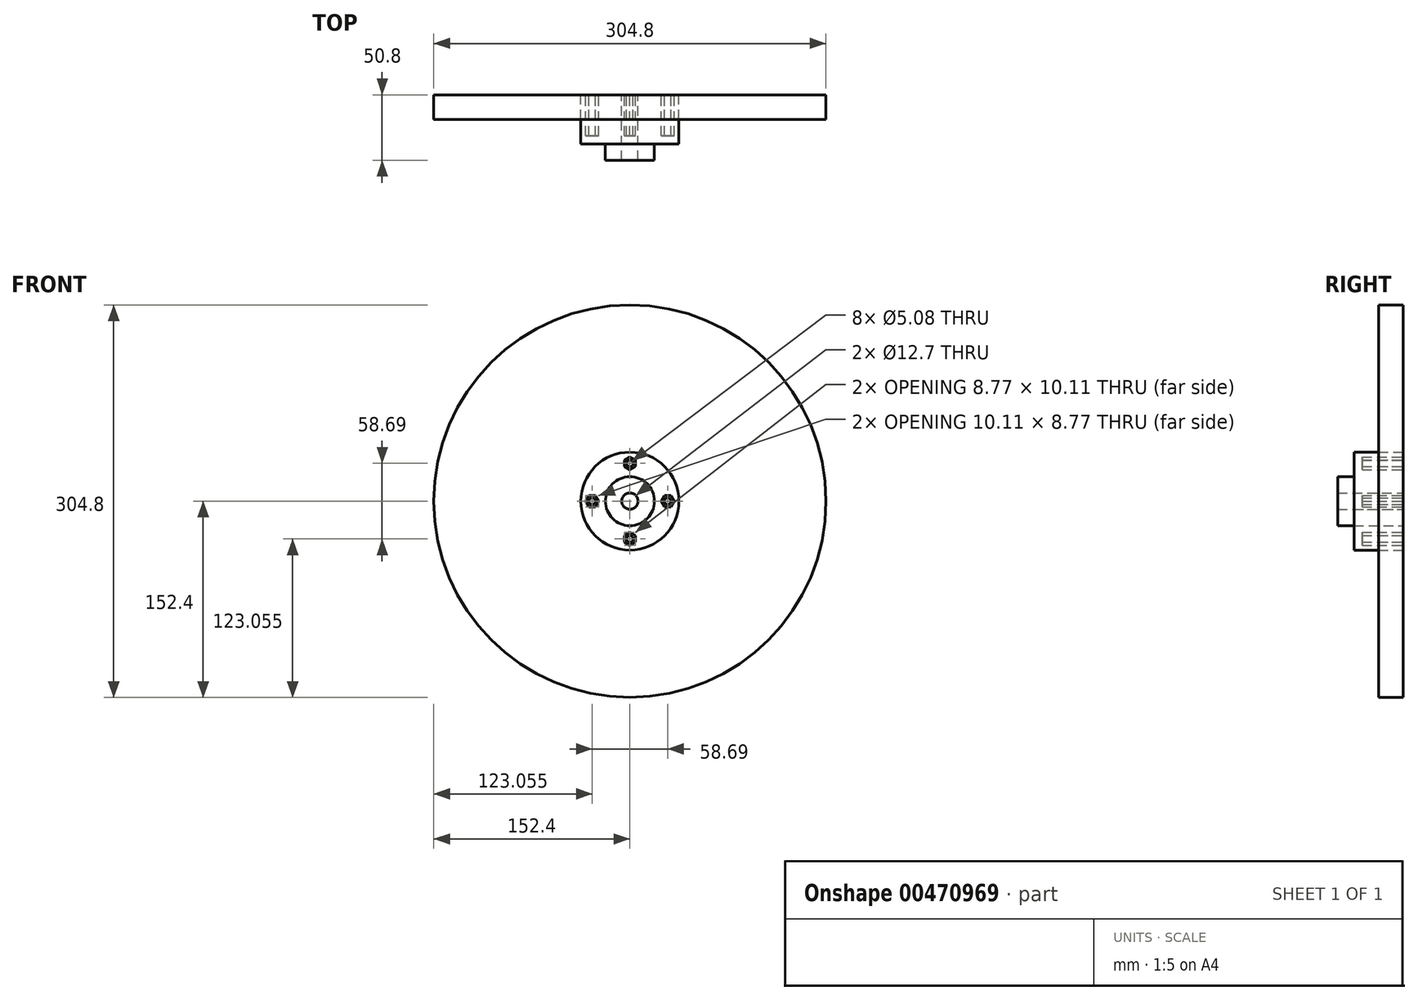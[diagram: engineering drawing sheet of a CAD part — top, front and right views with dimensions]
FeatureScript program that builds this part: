
annotation { "Feature Type Name" : "Feature", "Feature Type Description" : "" }
export const myFeature = defineFeature(function(context is Context, id is Id, definition is map)
    precondition{}
    {
        {
            var Q0;
            Q0=qCreatedBy(makeId("Front.planeOp"),FACE);
            var sketch = newSketch(context, id + "F0", { "sketchPlane" : qUnion([Q0])});
            skCircle(sketch, "E0", {"center": v(0, 0) * mm, "radius": 152.4 * mm});
            skCircle(sketch, "E1", {"center": v(0, 0) * mm, "radius": 38.1 * mm});
            skCircle(sketch, "E2", {"center": v(0, 0) * mm, "radius": 19.05 * mm});
            skCircle(sketch, "E3", {"center": v(0, 0) * mm, "radius": 6.35 * mm});
            skCircle(sketch, "E4.cCircle", {"center": v(-29.34, 0) * mm, "radius": 4.38 * mm, "construction": true});
            skLineSegment(sketch, "E4.0", {"start": v(-26.83, 4.39) * mm, "end": v(-24.3, 0.02) * mm});
            skLineSegment(sketch, "E4.1", {"start": v(-24.3, 0.02) * mm, "end": v(-26.8, -4.37) * mm});
            skLineSegment(sketch, "E4.2", {"start": v(-26.8, -4.37) * mm, "end": v(-31.85, -4.39) * mm});
            skLineSegment(sketch, "E4.3", {"start": v(-31.85, -4.39) * mm, "end": v(-34.4, -0.02) * mm});
            skLineSegment(sketch, "E4.4", {"start": v(-34.4, -0.02) * mm, "end": v(-31.89, 4.37) * mm});
            skLineSegment(sketch, "E4.5", {"start": v(-31.89, 4.37) * mm, "end": v(-26.83, 4.39) * mm});
            skPoint(sketch, "E4.0.midPoint", {"position": v(-25.56, 2.2) * mm});
            skLineSegment(sketch, "E5.1.0", {"start": v(4.39, -31.85) * mm, "end": v(0.02, -34.4) * mm});
            skLineSegment(sketch, "E5.1.1", {"start": v(4.37, -26.8) * mm, "end": v(4.39, -31.85) * mm});
            skLineSegment(sketch, "E5.1.2", {"start": v(-4.37, -31.89) * mm, "end": v(-4.39, -26.83) * mm});
            skLineSegment(sketch, "E5.1.3", {"start": v(-0.02, -24.3) * mm, "end": v(4.37, -26.8) * mm});
            skLineSegment(sketch, "E5.1.4", {"start": v(0.02, -34.4) * mm, "end": v(-4.37, -31.89) * mm});
            skCircle(sketch, "E5.1.5", {"center": v(0, -29.34) * mm, "radius": 4.38 * mm, "construction": true});
            skPoint(sketch, "E5.1.6", {"position": v(-2.2, -25.56) * mm});
            skLineSegment(sketch, "E5.1.7", {"start": v(-4.39, -26.83) * mm, "end": v(-0.02, -24.3) * mm});
            skLineSegment(sketch, "E5.2.0", {"start": v(31.85, 4.39) * mm, "end": v(34.4, 0.02) * mm});
            skLineSegment(sketch, "E5.2.1", {"start": v(26.8, 4.37) * mm, "end": v(31.85, 4.39) * mm});
            skLineSegment(sketch, "E5.2.2", {"start": v(31.89, -4.37) * mm, "end": v(26.83, -4.39) * mm});
            skLineSegment(sketch, "E5.2.3", {"start": v(24.3, -0.02) * mm, "end": v(26.8, 4.37) * mm});
            skLineSegment(sketch, "E5.2.4", {"start": v(34.4, 0.02) * mm, "end": v(31.89, -4.37) * mm});
            skCircle(sketch, "E5.2.5", {"center": v(29.34, 0) * mm, "radius": 4.38 * mm, "construction": true});
            skPoint(sketch, "E5.2.6", {"position": v(25.56, -2.2) * mm});
            skLineSegment(sketch, "E5.2.7", {"start": v(26.83, -4.39) * mm, "end": v(24.3, -0.02) * mm});
            skLineSegment(sketch, "E5.3.0", {"start": v(-4.39, 31.85) * mm, "end": v(-0.02, 34.4) * mm});
            skLineSegment(sketch, "E5.3.1", {"start": v(-4.37, 26.8) * mm, "end": v(-4.39, 31.85) * mm});
            skLineSegment(sketch, "E5.3.2", {"start": v(4.37, 31.89) * mm, "end": v(4.39, 26.83) * mm});
            skLineSegment(sketch, "E5.3.3", {"start": v(0.02, 24.3) * mm, "end": v(-4.37, 26.8) * mm});
            skLineSegment(sketch, "E5.3.4", {"start": v(-0.02, 34.4) * mm, "end": v(4.37, 31.89) * mm});
            skCircle(sketch, "E5.3.5", {"center": v(0, 29.34) * mm, "radius": 4.38 * mm, "construction": true});
            skPoint(sketch, "E5.3.6", {"position": v(2.2, 25.56) * mm});
            skLineSegment(sketch, "E5.3.7", {"start": v(4.39, 26.83) * mm, "end": v(0.02, 24.3) * mm});
            skCircle(sketch, "E6", {"center": v(-29.34, 0) * mm, "radius": 2.54 * mm});
            skCircle(sketch, "E7.1.0", {"center": v(0, -29.34) * mm, "radius": 2.54 * mm});
            skCircle(sketch, "E7.2.0", {"center": v(29.34, 0) * mm, "radius": 2.54 * mm});
            skCircle(sketch, "E7.3.0", {"center": v(0, 29.34) * mm, "radius": 2.54 * mm});
            skSolve(sketch);
        }
        {
            var Q0;
            Q0=makeQuery(id+"F0.imprint","IMPRINT",FACE,{"disambiguationData":[TD([[makeQuery(id+"F0.imprint","IMPRINT",EDGE,{"derivedFrom":sQuery(id+"F0.wireOp",EDGE,"E0")}),1.0]])]});
            var Q1;
            Q1=makeQuery(id+"F0.imprint","IMPRINT",FACE,{"disambiguationData":[TD([[makeQuery(id+"F0.imprint","IMPRINT",EDGE,{"derivedFrom":sQuery(id+"F0.wireOp",EDGE,"E1")}),1.0]])]});
            var Q2;
            Q2=makeQuery(id+"F0.imprint","IMPRINT",FACE,{"disambiguationData":[TD([[makeQuery(id+"F0.imprint","IMPRINT",EDGE,{"derivedFrom":sQuery(id+"F0.wireOp",EDGE,"E5.1.0")}),-1.0]])]});
            var Q3;
            Q3=makeQuery(id+"F0.imprint","IMPRINT",FACE,{"disambiguationData":[TD([[makeQuery(id+"F0.imprint","IMPRINT",EDGE,{"derivedFrom":sQuery(id+"F0.wireOp",EDGE,"E4.0")}),-1.0]])]});
            var Q4;
            Q4=makeQuery(id+"F0.imprint","IMPRINT",FACE,{"disambiguationData":[TD([[makeQuery(id+"F0.imprint","IMPRINT",EDGE,{"derivedFrom":sQuery(id+"F0.wireOp",EDGE,"E5.3.0")}),-1.0]])]});
            var Q5;
            Q5=makeQuery(id+"F0.imprint","IMPRINT",FACE,{"disambiguationData":[TD([[makeQuery(id+"F0.imprint","IMPRINT",EDGE,{"derivedFrom":sQuery(id+"F0.wireOp",EDGE,"E5.2.0")}),-1.0]])]});
            var Q6;
            Q6=makeQuery(id+"F0.imprint","IMPRINT",FACE,{"disambiguationData":[TD([[makeQuery(id+"F0.imprint","IMPRINT",EDGE,{"derivedFrom":sQuery(id+"F0.wireOp",EDGE,"E2")}),1.0]])]});
            var Q7;
            Q7=makeQuery(id+"F0.imprint","IMPRINT",FACE,{"disambiguationData":[TD([[makeQuery(id+"F0.imprint","IMPRINT",EDGE,{"derivedFrom":sQuery(id+"F0.wireOp",EDGE,"E3")}),1.0]])]});
            extrude(context, id + "F1", {"entities" : qUnion([Q0, Q1, Q2, Q3, Q4, Q5, Q6, Q7]), "depth" : 19.05 * mm});
        }
        {
            var Q0;
            Q0=makeQuery(id+"F0.imprint","IMPRINT",FACE,{"disambiguationData":[TD([[makeQuery(id+"F0.imprint","IMPRINT",EDGE,{"derivedFrom":sQuery(id+"F0.wireOp",EDGE,"E1")}),1.0]])]});
            var Q1;
            Q1=makeQuery(id+"F0.imprint","IMPRINT",FACE,{"disambiguationData":[TD([[makeQuery(id+"F0.imprint","IMPRINT",EDGE,{"derivedFrom":sQuery(id+"F0.wireOp",EDGE,"E2")}),1.0]])]});
            extrude(context, id + "F2", {"entities" : qUnion([Q0, Q1]), "depth" : 38.1 * mm});
        }
        {
            var Q0;
            Q0=makeQuery(id+"F0.imprint","IMPRINT",FACE,{"disambiguationData":[TD([[makeQuery(id+"F0.imprint","IMPRINT",EDGE,{"derivedFrom":sQuery(id+"F0.wireOp",EDGE,"E2")}),1.0]])]});
            extrude(context, id + "F3", {"entities" : qUnion([Q0]), "depth" : 50.8 * mm});
        }
        {
            var Q0;
            Q0=makeQuery(id+"F0.imprint","IMPRINT",FACE,{"disambiguationData":[TD([[makeQuery(id+"F0.imprint","IMPRINT",EDGE,{"derivedFrom":sQuery(id+"F0.wireOp",EDGE,"E4.0")}),-1.0]])]});
            var Q1;
            Q1=makeQuery(id+"F0.imprint","IMPRINT",FACE,{"disambiguationData":[TD([[makeQuery(id+"F0.imprint","IMPRINT",EDGE,{"derivedFrom":sQuery(id+"F0.wireOp",EDGE,"E5.1.0")}),-1.0]])]});
            var Q2;
            Q2=makeQuery(id+"F0.imprint","IMPRINT",FACE,{"disambiguationData":[TD([[makeQuery(id+"F0.imprint","IMPRINT",EDGE,{"derivedFrom":sQuery(id+"F0.wireOp",EDGE,"E5.2.0")}),-1.0]])]});
            var Q3;
            Q3=makeQuery(id+"F0.imprint","IMPRINT",FACE,{"disambiguationData":[TD([[makeQuery(id+"F0.imprint","IMPRINT",EDGE,{"derivedFrom":sQuery(id+"F0.wireOp",EDGE,"E5.3.0")}),-1.0]])]});
            extrude(context, id + "F4", {"entities" : qUnion([Q0, Q1, Q2, Q3]), "depth" : 31.75 * mm});
        }
    });
